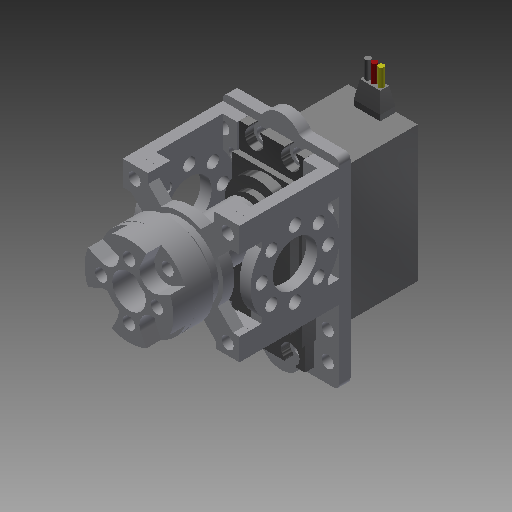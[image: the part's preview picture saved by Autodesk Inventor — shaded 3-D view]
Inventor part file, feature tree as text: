
AUTODESK INVENTOR PART (.ipt)
format: ipt  version: 2017 (Build 210142000, 142)  size: 798,208 bytes
history: native  units: in
note: dims shown in document units (in); Inventor stores cm internally (conversion verified against a paired STEP export)
features: extrude x23, sketch x23, other x11, projected_geometry x10, fillet x3, mirror x2, plane x1, pattern_circular x1
ambient origin geometry x8: Origin, YZ Plane, XZ Plane, XY Plane, X Axis, Y Axis, Z Axis, Center Point
bodies: Body1 (feature_tree), Body2 (feature_tree), Body3 (feature_tree), Body4 (feature_tree), Body5 (feature_tree), Body6 (feature_tree), Body7 (feature_tree), Body8 (feature_tree), Body9 (feature_tree), Body10 (feature_tree)
feature tree (74):
  other  "Servo"
  extrude  "Extrusion1"  Depth=1.525in
  extrude  "Extrusion2"  Depth=0.025in
  extrude  "Extrusion3"  Depth=0.17in
  fillet  "Fillet1"  Radius=0.11in
  plane  "Work Plane1"
  extrude  "Extrusion4"  Depth=0.07in
  fillet  "Fillet2"  Radius=0.07in
  mirror  "Mirror1"
  extrude  "Extrusion5"  [1 undecoded]
  extrude  "Extrusion6"  Depth=0.28in
  extrude  "Extrusion7"  Depth=0.1in
  extrude  "Extrusion8"  Depth=0.1in TaperAngle=0.0deg
  extrude  "Extrusion9"  Depth=0.3in
  extrude  "Extrusion10"  Depth=0.01in
  fillet  "Fillet3"  Radius=0.0625in
  extrude  "Extrusion11"  Depth=0.0625in
  extrude  "Extrusion12"  Depth=0.0625in
  extrude  "Extrusion13"  Depth=0.2in TaperAngle=0.0deg
  extrude  "Extrusion14"  Depth=0.0625in
  extrude  "Extrusion15"  Depth=0.2in
  extrude  "Extrusion16"  Depth=0.125in
  mirror  "Mirror2"
  extrude  "Extrusion18"  Depth=0.25in
  extrude  "Extrusion19"  Depth=0.125in
  extrude  "Extrusion20"  Depth=0.1325in
  extrude  "Extrusion21"  Depth=1.3125in
  extrude  "Extrusion22"  Depth=0.125in TaperAngle=0.0deg
  extrude  "Extrusion23"  Depth=0.125in
  extrude  "Extrusion24"  Depth=0.083in
  pattern_circular  "Circular Pattern1"  [2 undecoded]
  sketch  "Sketch1"  dims[d0=0.782in d1=1.525in]
  sketch  "Sketch2"  dims[d2=1.305in d3=0.0in d4=0.025in]
  sketch  "Sketch3"  dims[d5=0.025in d6=0.17in d7=0.11in d8=0.0in]
  sketch  "Sketch4"  dims[d9=0.508in d11=0.391in d12=0.07in d13=0.0in]
  sketch  "Sketch5"  dims[d14=0.366in d15=-0.16in]
  sketch  "Sketch6"  dims[d16=0.737in d18=0.28in]
  sketch  "Sketch7"  dims[d19=0.1in d20=0.21in d21=0.165in]
  other  "Red wire"
  sketch  "Sketch8"  dims[d22=0.165in d23=0.1in d24=0.0in]
  sketch  "Sketch9"  dims[d25=0.01in d26=0.3in]
  other  "Yellow Wire"
  sketch  "Sketch10"  dims[d27=0.17in d28=0.01in d29=0.0625in d30=0.0in]
  other  "BaseStructure"
  sketch  "Sketch11"  dims[d31=0.2in d32=-0.0687in d33=0.0625in]
  other  "ServoOutput"
  sketch  "Sketch12"  dims[d34=0.2in d35=0.0in d36=0.0625in]
  other  "SideStructure"
  sketch  "Sketch13"  dims[d37=0.04in d38=0.2in d39=0.0in]
  sketch  "Sketch14"  dims[d40=0.0625in d41=0.04in]
  projected_geometry  "Projected Loop1"
  projected_geometry  "Projected Loop2"
  sketch  "Sketch16"  dims[d42=0.2in d43=0.0in d44=0.136in]
  sketch  "Sketch17"  dims[d47=2.25in d48=0.125in]
  other  "Pattern of SideStructure:1"
  other  "SideStructureMirror"
  sketch  "Sketch18"  dims[d49=0.25in d50=0.25in]
  projected_geometry  "Projected Loop3"
  projected_geometry  "Projected Loop4"
  projected_geometry  "Projected Loop5"
  projected_geometry  "Projected Loop6"
  projected_geometry  "Projected Loop7"
  other  "BearingStructure"
  sketch  "Sketch19"  dims[d51=0.125in d52=0.2165in]
  sketch  "Sketch20"  dims[d53=0.1325in d54=0.1325in]
  other  "HubShaft"
  sketch  "Sketch21"  dims[d55=1.3125in d56=0.3125in]
  sketch  "Sketch22"  dims[d57=0.435in d58=0.125in d59=0.0in]
  sketch  "Sketch23"  dims[d60=0.0625in d61=0.125in]
  other  "HubAdapter"
  sketch  "Sketch24"  dims[d62=0.0625in d63=0.0in d66=0.083in d67=0.083in d68=0.125in d69=0.125in d70=0.125in d71=0.0in d72=0.125in d73=0.75in d74=0.0in d75=0.125in d76=0.0in d80=1.0in d82=0.125in d83=0.0in d84=0.5in d85=0.75in d86=0.136in d87=3.1496in d89=360.0deg d91=0.125in d92=0.0in d93=0.95in d94=45.0deg d96=0.26in d97=0.13in d100=45.0deg d101=0.13in d102=0.26in d103=0.125in d104=0.0in d105=0.845in d106=0.072in d107=0.0in d108=0.5in d109=0.8575in d110=0.0in d111=1.0in d112=0.75in d113=0.136in d114=3.1496in d116=360.0deg d118=0.2in d119=0.0in d120=0.3in d121=0.2in d122=0.0in d123=0.375in d124=0.625in d125=0.136in d126=1.5748in d128=360.0deg d130=0.25in d131=0.0in d133=0.1374in d134=0.1374in d135=0.168in d136=0.0in d137=1.5748in d138=360.0deg]
  projected_geometry  "Project Cut Edges1"
  projected_geometry  "Project Cut Edges2"
  projected_geometry  "Project Cut Edges3"
note: 3 required parameter values undecoded (feature->parameter linkage not recoverable at this tier; creation-order binding heuristic only, values carry confidence <= 0.55)
